# Revit family: Halter 35 quer gvz
name_source: partatom
category: HLS-Bauteile
revit_build: Autodesk Revit 2017 (Build: 20190507_1515(x64)
units: mm (PartAtom-declared; Revit-internal decimal feet)

## family parameters
Basisbauteil = Fläche
Beim Laden mit Abzugskörper schneiden = Nein
Bemaßung runder Anschluss = Durchmesser verwenden
Gemeinsam genutzt = Ja
Raumberechnungspunkt = Nein
Teiletyp = Normal

## types (1)
- Halter 35 quer gvz
    Anzugsmoment = 0.00 kip-ft
    Artikelnummer = 080213502
    Breite = 0 mm  [stored 0 ft]
    Fabrikat = MEFA
    Firma = MEFA Befestigungs- und Montagesysteme GmbH
    Gewicht = 0.37 kg
    Gewicht pro Bauteil = 0.37 kg
    Kurztext1 = Halter C-Profil 35 quer
    Kurztext2 = für C-Profil 35, Stex 35 gvz
    Langloch = 11x15 mm
    Länge = 0 mm  [stored 0 ft]
    Material = Stahl
    Materialname = S235
    Oberflaeche = galvanisch verzinkt
    Profiltyp = 35, Stex 35
    Stärke Material = 0 mm  [stored 0 ft]
    Vorgabe-Ansicht = 1219 mm
    max. zul. Last = 0.45 kip
    vpe = 25 St

note: [stored X ft] marks values corroborated as IEEE doubles in the binary element streams (Revit-internal decimal feet)
